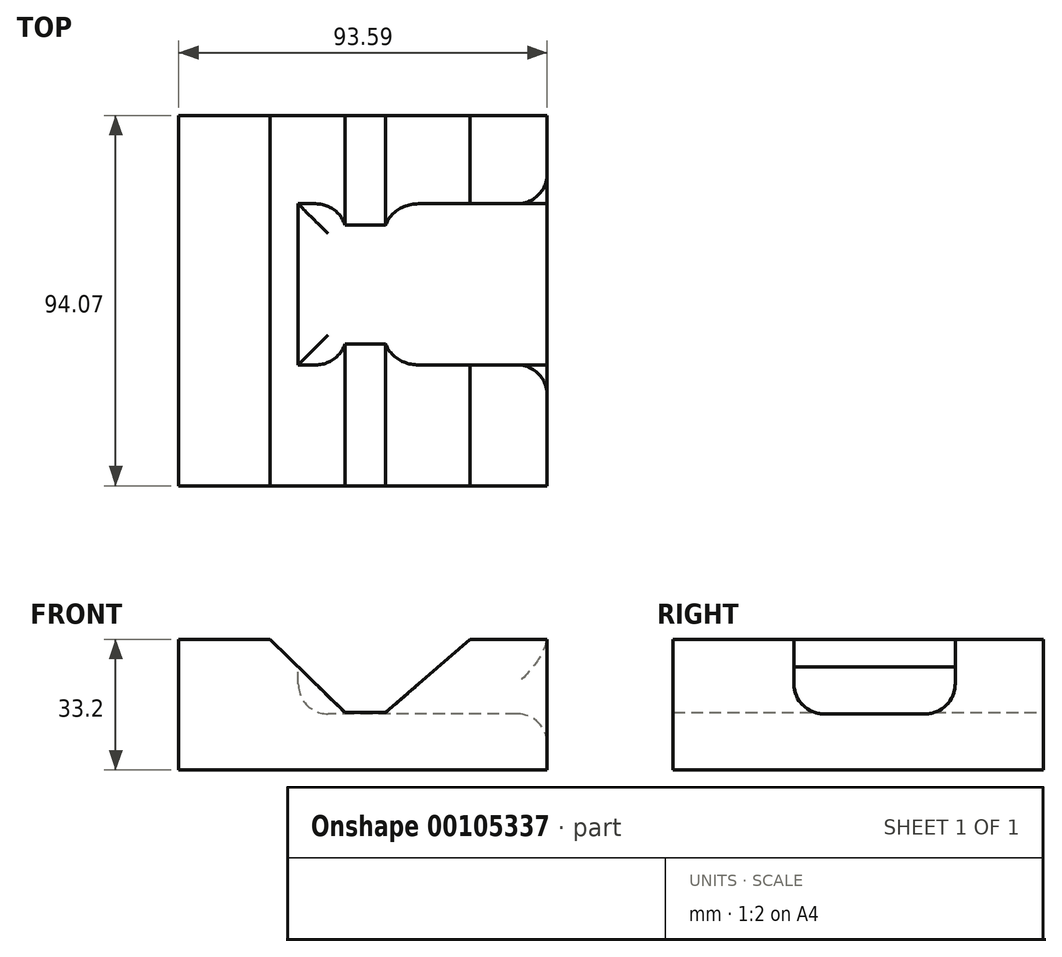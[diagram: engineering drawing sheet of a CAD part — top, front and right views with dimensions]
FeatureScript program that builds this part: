
annotation { "Feature Type Name" : "Feature", "Feature Type Description" : "" }
export const myFeature = defineFeature(function(context is Context, id is Id, definition is map)
    precondition{}
    {
        {
            var Q0;
            Q0=qCreatedBy(makeId("Top.planeOp"),FACE);
            var sketch = newSketch(context, id + "F0", { "sketchPlane" : qUnion([Q0])});
            skLineSegment(sketch, "E0.bottom", {"start": v(-52.55, 49.19) * mm, "end": v(41.04, 49.19) * mm});
            skLineSegment(sketch, "E0.top", {"start": v(-52.55, -44.88) * mm, "end": v(41.04, -44.88) * mm});
            skLineSegment(sketch, "E0.left", {"start": v(-52.55, 49.19) * mm, "end": v(-52.55, -44.88) * mm});
            skLineSegment(sketch, "E0.right", {"start": v(41.04, 49.19) * mm, "end": v(41.04, -44.88) * mm});
            skSolve(sketch);
        }
        {
            var Q0;
            Q0 = qSketchRegion(id + "F0", true);
            extrude(context, id + "F1", {"entities" : qUnion([Q0]), "oppositeDirection" : true, "depth" : 33.2 * mm});
        }
        {
            var Q0;
            Q0=makeQuery(id+"F1.opExtrude","CAP_FACE",FACE,{"disambiguationData":[OSD([sQuery(id+"F0.wireOp",EDGE,"E0.bottom"),sQuery(id+"F0.wireOp",EDGE,"E0.top"),sQuery(id+"F0.wireOp",EDGE,"E0.left"),sQuery(id+"F0.wireOp",EDGE,"E0.right")])],"isStart":true});
            var sketch = newSketch(context, id + "F2", { "sketchPlane" : qUnion([Q0])});
            skLineSegment(sketch, "E1.bottom", {"start": v(41.04, -14.17) * mm, "end": v(-22.22, -14.17) * mm});
            skLineSegment(sketch, "E1.top", {"start": v(41.04, 26.77) * mm, "end": v(-22.22, 26.77) * mm});
            skLineSegment(sketch, "E1.left", {"start": v(41.04, -14.17) * mm, "end": v(41.04, 26.77) * mm});
            skLineSegment(sketch, "E1.right", {"start": v(-22.22, -14.17) * mm, "end": v(-22.22, 26.77) * mm});
            skSolve(sketch);
        }
        {
            var Q0;
            Q0 = qSketchRegion(id + "F2", true);
            extrude(context, id + "F3", {"entities" : qUnion([Q0]), "operationType" : NewBodyOperationType.REMOVE, "oppositeDirection" : true, "depth" : 18.96 * mm});
        }
        {
            var Q0;
            Q0=makeQuery(id+"F3.boolean.opBoolean","COPY",FACE,{"derivedFrom":makeQuery(id+"F3.opExtrude","CAP_FACE",FACE,{"disambiguationData":[OSD([sQuery(id+"F2.wireOp",EDGE,"E1.bottom"),sQuery(id+"F2.wireOp",EDGE,"E1.top"),sQuery(id+"F2.wireOp",EDGE,"E1.left"),sQuery(id+"F2.wireOp",EDGE,"E1.right")])],"isStart":false})});
            var Q1;
            Q1=makeQuery(id+"F3.boolean.opBoolean","COPY",EDGE,{"derivedFrom":makeQuery(id+"F3.opExtrude","CAP_EDGE",EDGE,{"disambiguationData":[OSD([sQuery(id+"F2.wireOp",EDGE,"E1.right")])],"isStart":true})});
            fillet(context, id + "F4", {"entities" : qUnion([Q0, Q1]), "radius" : 7.62 * mm, "tangentPropagation" : true, "allowEdgeOverflow" : false});
        }
        {
            var Q0;
            Q0=makeQuery(id+"F1.opExtrude","SWEPT_FACE",FACE,{"disambiguationData":[OSD([sQuery(id+"F0.wireOp",EDGE,"E0.bottom")])]});
            var sketch = newSketch(context, id + "F5", { "sketchPlane" : qUnion([Q0])});
            skLineSegment(sketch, "E2", {"start": v(-21.4, 0) * mm, "end": v(0, -18.62) * mm});
            skLineSegment(sketch, "E3", {"start": v(0, -18.62) * mm, "end": v(10.34, -18.62) * mm});
            skLineSegment(sketch, "E4", {"start": v(10.34, -18.62) * mm, "end": v(29.34, 0) * mm});
            skLineSegment(sketch, "E5", {"start": v(29.34, 0) * mm, "end": v(-21.4, 0) * mm});
            skSolve(sketch);
        }
        {
            var Q0;
            Q0=makeQuery(id+"F5.imprint","IMPRINT",FACE,{"disambiguationData":[TD([[makeQuery(id+"F5.imprint","IMPRINT",EDGE,{"derivedFrom":sQuery(id+"F5.wireOp",EDGE,"E2")}),1.0]])]});
            extrude(context, id + "F6", {"entities" : qUnion([Q0]), "operationType" : NewBodyOperationType.REMOVE, "oppositeDirection" : true, "depth" : 123.1 * mm});
        }
    });
